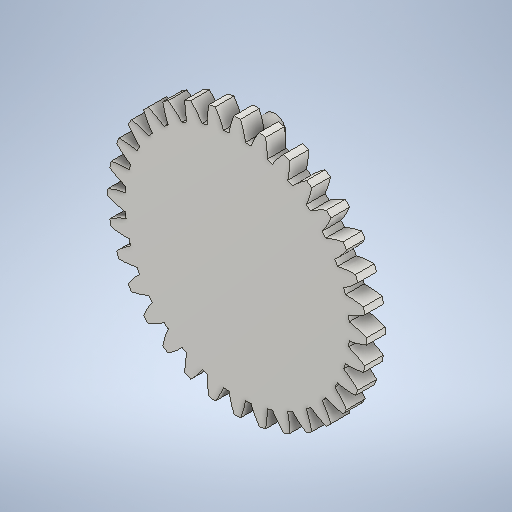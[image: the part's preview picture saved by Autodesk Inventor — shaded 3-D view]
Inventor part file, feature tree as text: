
AUTODESK INVENTOR PART (.ipt)
format: ipt  version: 2025.1 (Build 291241000, 241)  size: 450,560 bytes
history: native  units: mm (DEFAULTED — no unit token found)
features: sketch x4, extrude x3, plane x3, other x3
ambient origin geometry x8: Origin, YZ Plane, XZ Plane, XY Plane, X Axis, Y Axis, Z Axis, Center Point
bodies: Solid1 (feature_tree)
feature tree (13):
  extrude  "Extrusion1"  Depth=5.0mm TaperAngle=0.0deg
  plane  "Work Plane2"
  plane  "Work Plane8"
  plane  "Work Plane9"
  other  "Spur Gear"
  sketch  "Sketch6"  dims[d16=33.495mm d17=0.0mm d34=0.981748mm]
  extrude  "Extrusion3"  Depth=10.0mm TaperAngle=0.0deg
  extrude  "Extrusion2"  Depth=0.981748mm TaperAngle=0.0deg
  sketch  "Sketch1"  dims[d0=69.02mm d1=5.0mm d2=0.0mm]
  other  "Srf1"
  sketch  "Sketch4"  dims[d3=64.96mm d4=10.0mm d5=0.0mm]
  sketch  "Sketch7"  dims[d39=0.0mm d41=0.0mm d43=33.495mm d46=33.495mm d47=0.0mm d48=0.0mm d52=10.0mm d53=0.0mm d54=65.0mm d55=5.0mm d56=6.0mm d57=5.0mm d58=27.5mm d59=5.0mm d60=0.0mm]
  other  "Pitch Diameter"
